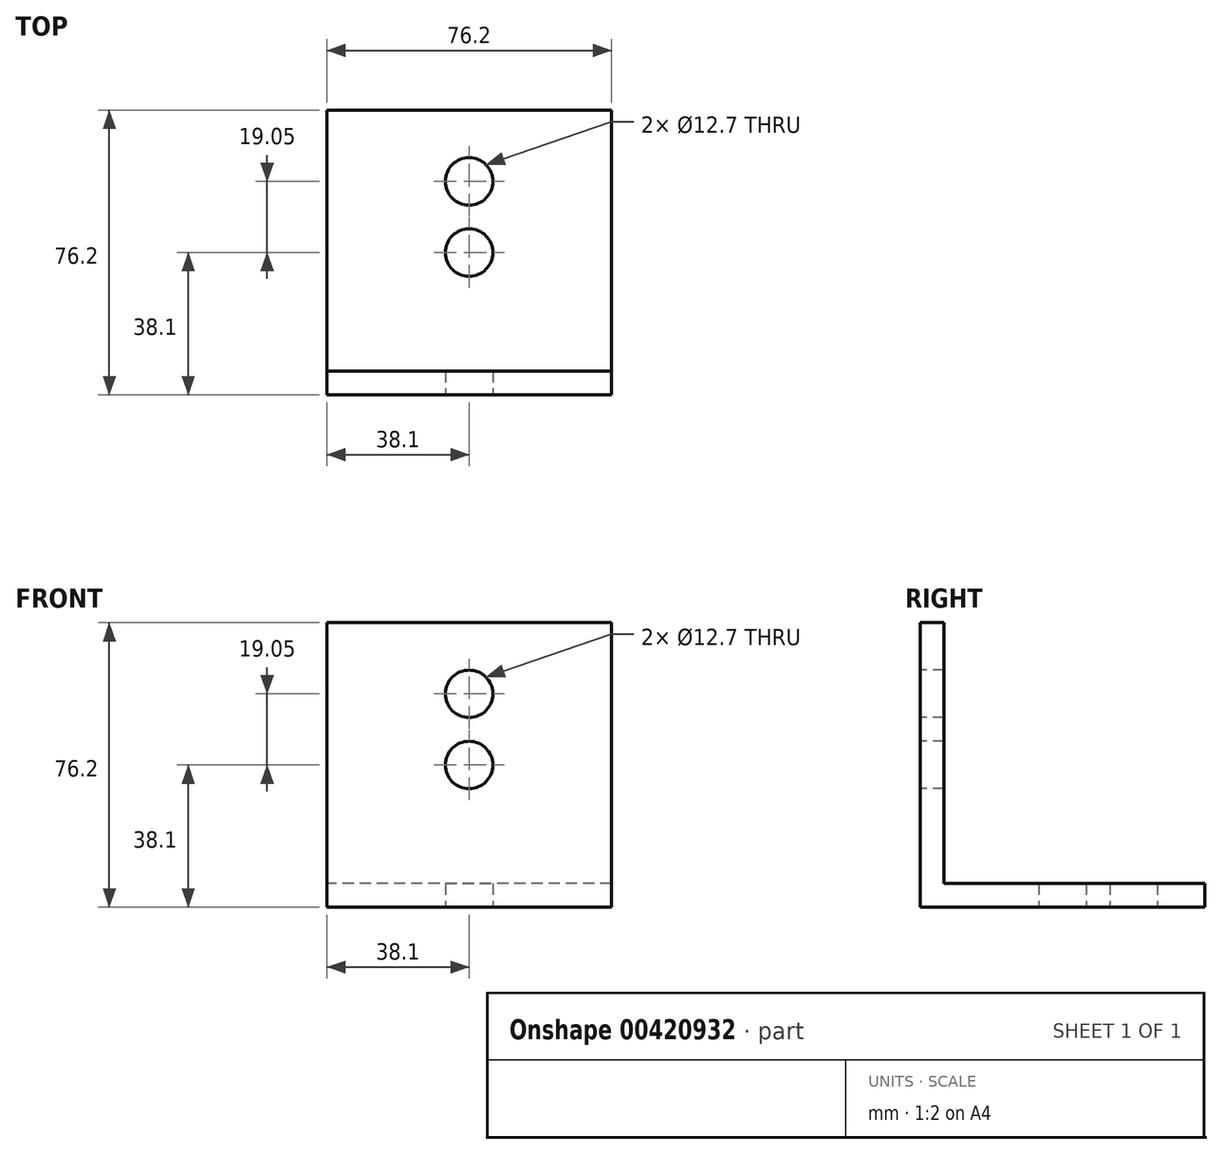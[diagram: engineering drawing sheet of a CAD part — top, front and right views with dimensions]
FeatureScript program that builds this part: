
annotation { "Feature Type Name" : "Feature", "Feature Type Description" : "" }
export const myFeature = defineFeature(function(context is Context, id is Id, definition is map)
    precondition{}
    {
        {
            var Q0;
            Q0=qCreatedBy(makeId("Right.planeOp"),FACE);
            var sketch = newSketch(context, id + "F0", { "sketchPlane" : qUnion([Q0])});
            skLineSegment(sketch, "E0", {"start": v(0, 0) * mm, "end": v(76.2, 0) * mm});
            skLineSegment(sketch, "E1", {"start": v(76.2, 0) * mm, "end": v(76.2, 6.35) * mm});
            skLineSegment(sketch, "E2", {"start": v(76.2, 6.35) * mm, "end": v(6.35, 6.35) * mm});
            skLineSegment(sketch, "E3", {"start": v(6.35, 6.35) * mm, "end": v(6.35, 76.2) * mm});
            skLineSegment(sketch, "E4", {"start": v(6.35, 76.2) * mm, "end": v(0, 76.2) * mm});
            skLineSegment(sketch, "E5", {"start": v(0, 76.2) * mm, "end": v(0, 0) * mm});
            skSolve(sketch);
        }
        {
            var Q0;
            Q0 = qSketchRegion(id + "F0", true);
            extrude(context, id + "F1", {"entities" : qUnion([Q0]), "depth" : 76.2 * mm});
        }
        {
            var Q0;
            Q0=qCreatedBy(makeId("Front.planeOp"),FACE);
            var sketch = newSketch(context, id + "F2", { "sketchPlane" : qUnion([Q0])});
            skCircle(sketch, "E6", {"center": v(38.1, 57.15) * mm, "radius": 6.35 * mm});
            skCircle(sketch, "E7", {"center": v(38.1, 38.1) * mm, "radius": 6.35 * mm});
            skSolve(sketch);
        }
        {
            var Q0;
            Q0 = qSketchRegion(id + "F2", true);
            extrude(context, id + "F3", {"entities" : qUnion([Q0]), "operationType" : NewBodyOperationType.REMOVE, "endBound" : BoundingType.THROUGH_ALL, "oppositeDirection" : true, "depth" : 25.4 * mm});
        }
        {
            var Q0;
            Q0=qCreatedBy(makeId("Top.planeOp"),FACE);
            var sketch = newSketch(context, id + "F4", { "sketchPlane" : qUnion([Q0])});
            skCircle(sketch, "E8", {"center": v(38.1, 38.1) * mm, "radius": 6.35 * mm});
            skCircle(sketch, "E9", {"center": v(38.1, 57.15) * mm, "radius": 6.35 * mm});
            skSolve(sketch);
        }
        {
            var Q0;
            Q0 = qSketchRegion(id + "F4", true);
            extrude(context, id + "F5", {"entities" : qUnion([Q0]), "operationType" : NewBodyOperationType.REMOVE, "endBound" : BoundingType.THROUGH_ALL, "depth" : 25.4 * mm});
        }
    });
